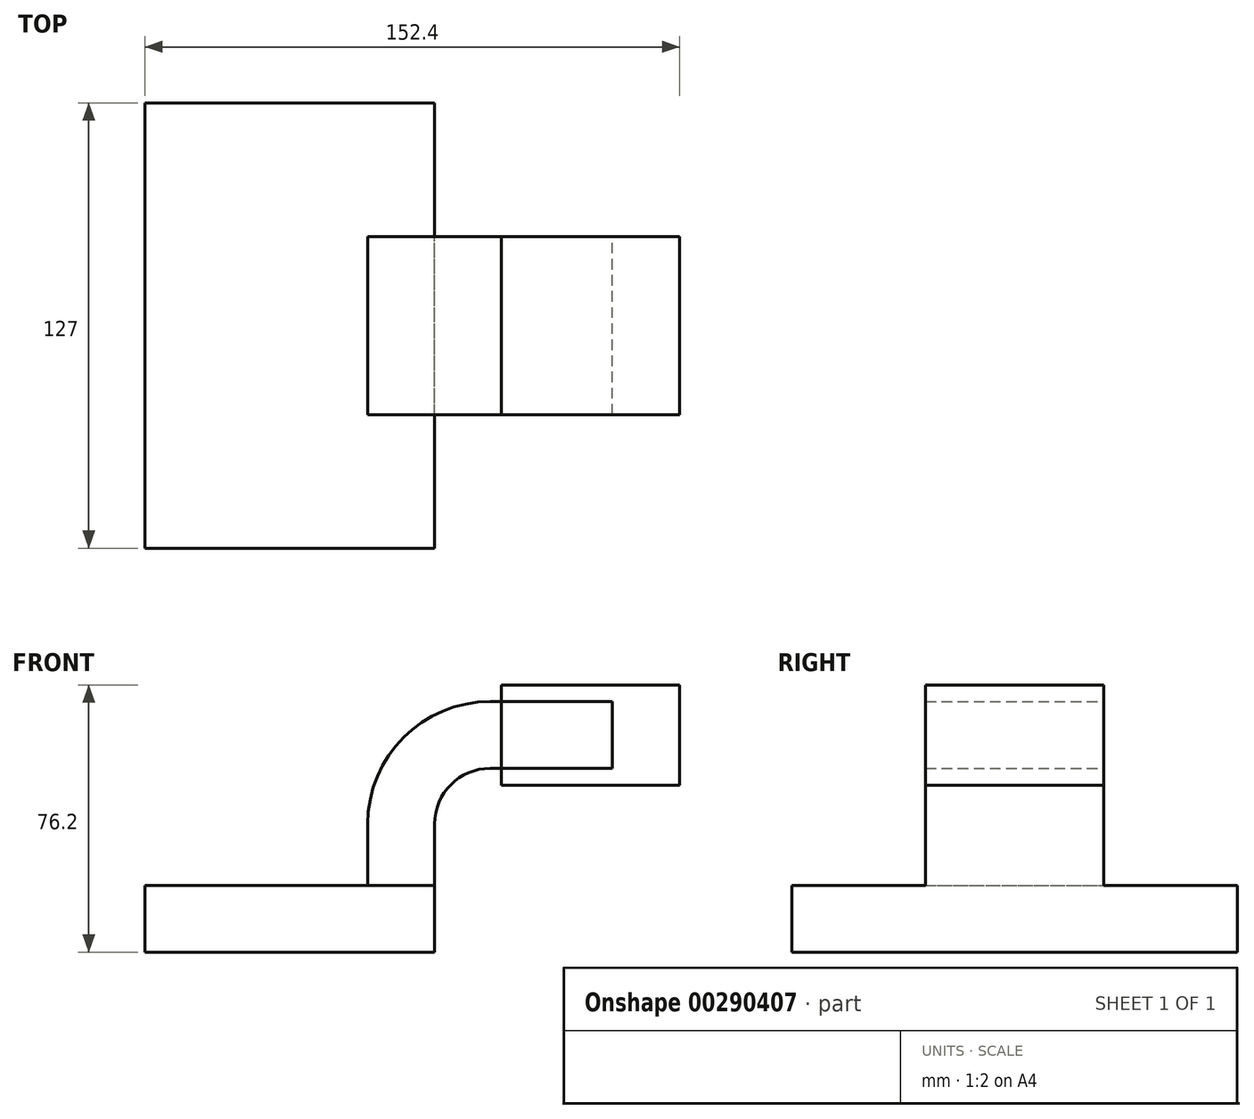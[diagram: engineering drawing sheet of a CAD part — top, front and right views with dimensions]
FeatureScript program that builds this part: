
annotation { "Feature Type Name" : "Feature", "Feature Type Description" : "" }
export const myFeature = defineFeature(function(context is Context, id is Id, definition is map)
    precondition{}
    {
        {
            var Q0;
            Q0=qCreatedBy(makeId("Front.planeOp"),FACE);
            var sketch = newSketch(context, id + "F0", { "sketchPlane" : qUnion([Q0])});
            skLineSegment(sketch, "E0.bottom", {"start": v(41.28, -9.52) * mm, "end": v(-41.28, -9.53) * mm});
            skLineSegment(sketch, "E0.top", {"start": v(41.28, 9.53) * mm, "end": v(-41.28, 9.53) * mm});
            skLineSegment(sketch, "E0.left", {"start": v(41.28, -9.52) * mm, "end": v(41.28, 9.53) * mm});
            skLineSegment(sketch, "E0.right", {"start": v(-41.28, -9.53) * mm, "end": v(-41.28, 9.53) * mm});
            skPoint(sketch, "E0.middle", {"position": v(0, 0) * mm});
            skLineSegment(sketch, "E1.bottom", {"start": v(111.12, 38.1) * mm, "end": v(60.32, 38.1) * mm});
            skLineSegment(sketch, "E1.top", {"start": v(111.12, 66.68) * mm, "end": v(60.32, 66.68) * mm});
            skLineSegment(sketch, "E1.left", {"start": v(111.12, 38.1) * mm, "end": v(111.12, 66.68) * mm});
            skLineSegment(sketch, "E1.right", {"start": v(60.32, 38.1) * mm, "end": v(60.32, 66.68) * mm});
            skPoint(sketch, "E1.middle", {"position": v(85.72, 52.39) * mm});
            skLineSegment(sketch, "E2", {"start": v(41.28, 9.53) * mm, "end": v(41.28, 27) * mm});
            skArc(sketch, "E3", {"start": v(41.27, 27) * mm, "mid": v(45.92, 38.23) * mm, "end": v(57.15, 42.88) * mm});
            skLineSegment(sketch, "E4", {"start": v(57.15, 42.88) * mm, "end": v(91.9, 42.88) * mm});
            skLineSegment(sketch, "E5", {"start": v(91.9, 42.88) * mm, "end": v(74.52, 42.88) * mm});
            skLineSegment(sketch, "E6.0", {"start": v(57.15, 61.93) * mm, "end": v(91.9, 61.93) * mm});
            skArc(sketch, "E6.1", {"start": v(22.23, 27) * mm, "mid": v(32.45, 51.7) * mm, "end": v(57.15, 61.93) * mm});
            skLineSegment(sketch, "E6.2", {"start": v(22.22, 9.53) * mm, "end": v(22.22, 27) * mm});
            skLineSegment(sketch, "E7", {"start": v(91.9, 42.88) * mm, "end": v(91.9, 61.93) * mm});
            skFitSpline(sketch, "E8", {"points": [v(-41.28, 9.53) * mm, v(57.15, 61.93) * mm], "startDerivative": vector(38.6, 130.92) * mm, "endDerivative": vector(55.1, -10.83) * mm});
            skSolve(sketch);
        }
        {
            var Q0;
            Q0=makeQuery(id+"F0.imprint","IMPRINT",FACE,{"disambiguationData":[TD([[makeQuery(id+"F0.imprint","IMPRINT",EDGE,{"derivedFrom":sQuery(id+"F0.wireOp",EDGE,"E0.bottom")}),-1.0]])]});
            extrude(context, id + "F1", {"entities" : qUnion([Q0]), "endBound" : BoundingType.SYMMETRIC, "depth" : 127 * mm});
        }
        {
            var Q0;
            {var subQ1=sQuery(id+"F0.wireOp",EDGE,"E2");Q0=makeQuery(id+"F0.imprint","IMPRINT",FACE,{"disambiguationData":[TD([[makeQuery(id+"F0.imprint","IMPRINT",EDGE,{"derivedFrom":subQ1}),1.0]])]});}
            var Q1;
            {var subQ4=sQuery(id+"F0.wireOp",EDGE,"E5");Q1=makeQuery(id+"F0.imprint","IMPRINT",FACE,{"disambiguationData":[TD([[makeQuery(id+"F0.imprint","IMPRINT",EDGE,{"derivedFrom":subQ4}),-1.0]])]});}
            var Q2;
            {var subQ1=sQuery(id+"F0.wireOp",EDGE,"E1.bottom");Q2=makeQuery(id+"F0.imprint","IMPRINT",FACE,{"disambiguationData":[TD([[makeQuery(id+"F0.imprint","IMPRINT",EDGE,{"derivedFrom":subQ1}),-1.0]])]});}
            extrude(context, id + "F2", {"entities" : qUnion([Q0, Q1, Q2]), "operationType" : NewBodyOperationType.ADD, "endBound" : BoundingType.SYMMETRIC, "depth" : 50.8 * mm});
        }
        {
            var Q0;
            Q0=makeQuery(id+"F0.imprint","IMPRINT",FACE,{"disambiguationData":[TD([[makeQuery(id+"F0.imprint","IMPRINT",EDGE,{"derivedFrom":sQuery(id+"F0.wireOp",EDGE,"E6.1")}),1.0]])]});
            extrude(context, id + "F3", {"entities" : qUnion([Q0]), "operationType" : NewBodyOperationType.ADD, "endBound" : BoundingType.SYMMETRIC, "depth" : 15.88 * mm});
        }
    });
